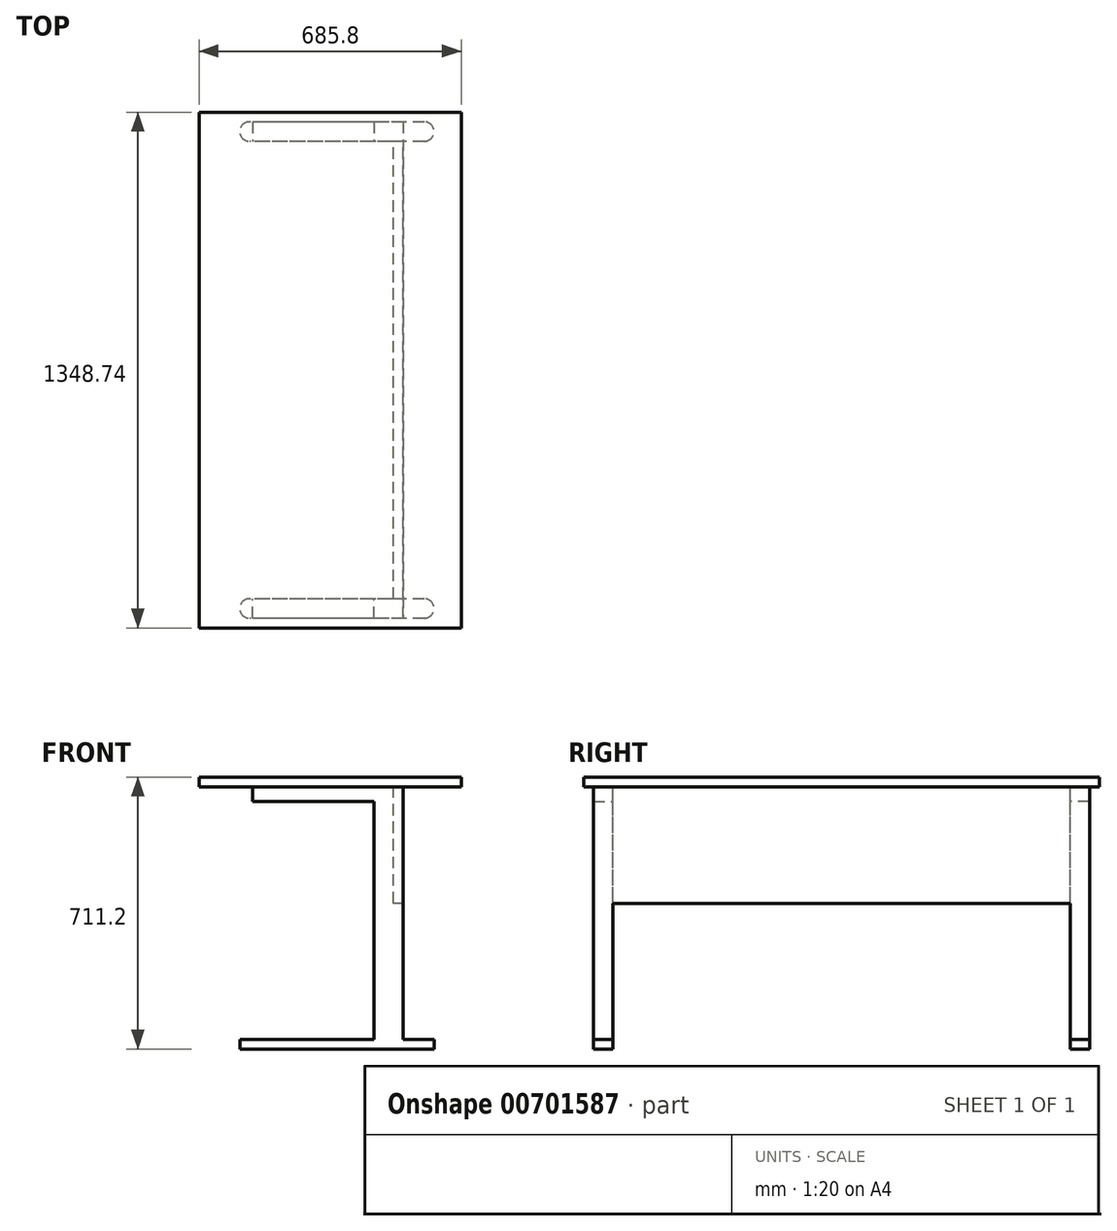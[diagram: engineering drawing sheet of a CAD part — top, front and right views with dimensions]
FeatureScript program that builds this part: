
annotation { "Feature Type Name" : "Feature", "Feature Type Description" : "" }
export const myFeature = defineFeature(function(context is Context, id is Id, definition is map)
    precondition{}
    {
        {
            var Q0;
            Q0=qCreatedBy(makeId("Top.planeOp"),FACE);
            var sketch = newSketch(context, id + "F0", { "sketchPlane" : qUnion([Q0])});
            skLineSegment(sketch, "E0.bottom", {"start": v(-342.9, 674.37) * mm, "end": v(342.9, 674.37) * mm});
            skLineSegment(sketch, "E0.top", {"start": v(-342.9, -674.37) * mm, "end": v(342.9, -674.37) * mm});
            skLineSegment(sketch, "E0.left", {"start": v(-342.9, 674.37) * mm, "end": v(-342.9, -674.37) * mm});
            skLineSegment(sketch, "E0.right", {"start": v(342.9, 674.37) * mm, "end": v(342.9, -674.37) * mm});
            skPoint(sketch, "E0.middle", {"position": v(0, 0) * mm});
            skSolve(sketch);
        }
        {
            var Q0;
            Q0=qSketchRegion(id+"F0",true);
            extrude(context, id + "F1", {"entities" : qUnion([Q0]), "depth" : 25.4 * mm, "offsetDistance" : 25.4 * mm});
        }
        {
            var Q0;
            Q0=makeQuery(id+"F1.opExtrude","CAP_FACE",FACE,{"disambiguationData":[OSD([sQuery(id+"F0.wireOp",EDGE,"E0.bottom"),sQuery(id+"F0.wireOp",EDGE,"E0.top"),sQuery(id+"F0.wireOp",EDGE,"E0.left"),sQuery(id+"F0.wireOp",EDGE,"E0.right")])],"isStart":true});
            var sketch = newSketch(context, id + "F2", { "sketchPlane" : qUnion([Q0])});
            skLineSegment(sketch, "E1", {"start": v(289.24, 0) * mm, "end": v(-342.9, 0) * mm});
            skLineSegment(sketch, "E2", {"start": v(-342.9, 0) * mm, "end": v(342.9, 0) * mm});
            skLineSegment(sketch, "E3.bottom", {"start": v(114.3, -648.97) * mm, "end": v(-203.2, -648.97) * mm});
            skLineSegment(sketch, "E3.top", {"start": v(114.3, -598.17) * mm, "end": v(-203.2, -598.17) * mm});
            skLineSegment(sketch, "E3.left", {"start": v(114.3, -648.97) * mm, "end": v(114.3, -598.17) * mm});
            skLineSegment(sketch, "E3.right", {"start": v(-203.2, -648.97) * mm, "end": v(-203.2, -598.17) * mm});
            skLineSegment(sketch, "E4.MirrorCS", {"start": v(114.3, 648.97) * mm, "end": v(-203.2, 648.97) * mm});
            skLineSegment(sketch, "E5.MirrorCS", {"start": v(114.3, 598.17) * mm, "end": v(-203.2, 598.17) * mm});
            skLineSegment(sketch, "E6.MirrorCS", {"start": v(-203.2, 648.97) * mm, "end": v(-203.2, 598.17) * mm});
            skLineSegment(sketch, "E7.MirrorCS", {"start": v(114.3, 648.97) * mm, "end": v(114.3, 598.17) * mm});
            skSolve(sketch);
        }
        {
            var Q0;
            Q0=qSketchRegion(id+"F2",true);
            extrude(context, id + "F3", {"entities" : qUnion([Q0]), "operationType" : NewBodyOperationType.ADD, "depth" : 38.1 * mm, "offsetDistance" : 25.4 * mm});
        }
        {
            var Q0;
            Q0=makeQuery(id+"F1.opExtrude","CAP_FACE",FACE,{"disambiguationData":[OSD([sQuery(id+"F0.wireOp",EDGE,"E0.bottom"),sQuery(id+"F0.wireOp",EDGE,"E0.top"),sQuery(id+"F0.wireOp",EDGE,"E0.left"),sQuery(id+"F0.wireOp",EDGE,"E0.right")])],"isStart":true});
            var sketch = newSketch(context, id + "F4", { "sketchPlane" : qUnion([Q0])});
            skLineSegment(sketch, "E8.bottom", {"start": v(114.3, -648.97) * mm, "end": v(190.5, -648.97) * mm});
            skLineSegment(sketch, "E8.top", {"start": v(114.3, -598.17) * mm, "end": v(190.5, -598.17) * mm});
            skLineSegment(sketch, "E8.left", {"start": v(114.3, -648.97) * mm, "end": v(114.3, -598.17) * mm});
            skLineSegment(sketch, "E8.right", {"start": v(190.5, -648.97) * mm, "end": v(190.5, -598.17) * mm});
            skLineSegment(sketch, "E9", {"start": v(298.65, 0) * mm, "end": v(-342.9, 0) * mm});
            skLineSegment(sketch, "E10", {"start": v(-342.9, 0) * mm, "end": v(342.9, 0) * mm});
            skLineSegment(sketch, "E11.MirrorCS", {"start": v(114.3, 648.97) * mm, "end": v(190.5, 648.97) * mm});
            skLineSegment(sketch, "E12.MirrorCS", {"start": v(114.3, 598.17) * mm, "end": v(190.5, 598.17) * mm});
            skLineSegment(sketch, "E13.MirrorCS", {"start": v(190.5, 648.97) * mm, "end": v(190.5, 598.17) * mm});
            skLineSegment(sketch, "E14", {"start": v(114.3, 623.57) * mm, "end": v(114.3, 648.97) * mm});
            skLineSegment(sketch, "E15", {"start": v(114.3, 609.27) * mm, "end": v(114.3, 598.17) * mm});
            skLineSegment(sketch, "E16", {"start": v(114.3, 609.27) * mm, "end": v(114.3, 623.57) * mm});
            skSolve(sketch);
        }
        {
            var Q0;
            Q0=makeQuery(id+"F4.imprint","IMPRINT",FACE,{"disambiguationData":[TD([[makeQuery(id+"F4.imprint","IMPRINT",EDGE,{"derivedFrom":sQuery(id+"F4.wireOp",EDGE,"E8.bottom")}),1.0]])]});
            var Q1;
            Q1=qSketchRegion(id+"F4",true);
            extrude(context, id + "F5", {"entities" : qUnion([Q0, Q1]), "operationType" : NewBodyOperationType.ADD, "depth" : 660.4 * mm, "offsetDistance" : 25.4 * mm});
        }
        {
            var Q0;
            Q0=makeQuery(id+"F5.opExtrude","CAP_FACE",FACE,{"disambiguationData":[OSD([sQuery(id+"F4.wireOp",EDGE,"E8.bottom"),sQuery(id+"F4.wireOp",EDGE,"E8.top"),sQuery(id+"F4.wireOp",EDGE,"E8.left"),sQuery(id+"F4.wireOp",EDGE,"E8.right")])],"isStart":false});
            var sketch = newSketch(context, id + "F6", { "sketchPlane" : qUnion([Q0])});
            skLineSegment(sketch, "E17.bottom", {"start": v(246.19, -598.17) * mm, "end": v(-211.01, -598.17) * mm});
            skLineSegment(sketch, "E17.top", {"start": v(246.19, -648.97) * mm, "end": v(-211.01, -648.97) * mm});
            skLineSegment(sketch, "E17.left", {"start": v(271.59, -623.57) * mm, "end": v(271.59, -623.57) * mm});
            skLineSegment(sketch, "E17.right", {"start": v(-236.41, -623.57) * mm, "end": v(-236.41, -623.57) * mm});
            skPoint(sketch, "E18.visualSharp", {"position": v(271.59, -648.97) * mm});
            skArc(sketch, "E18.filletArc", {"start": v(246.19, -648.97) * mm, "mid": v(264.15, -641.53) * mm, "end": v(271.59, -623.57) * mm});
            skPoint(sketch, "E19.visualSharp", {"position": v(271.59, -598.17) * mm});
            skArc(sketch, "E19.filletArc", {"start": v(271.59, -623.57) * mm, "mid": v(264.15, -605.6) * mm, "end": v(246.19, -598.17) * mm});
            skPoint(sketch, "E20.visualSharp", {"position": v(-236.41, -648.97) * mm});
            skArc(sketch, "E20.filletArc", {"start": v(-236.41, -623.57) * mm, "mid": v(-228.97, -641.53) * mm, "end": v(-211.01, -648.97) * mm});
            skPoint(sketch, "E21.visualSharp", {"position": v(-236.41, -598.17) * mm});
            skArc(sketch, "E21.filletArc", {"start": v(-211.01, -598.17) * mm, "mid": v(-228.97, -605.6) * mm, "end": v(-236.41, -623.57) * mm});
            skLineSegment(sketch, "E22", {"start": v(-361.07, 0) * mm, "end": v(355.78, 0) * mm});
            skArc(sketch, "E23.MirrorCS", {"start": v(-211.01, 598.17) * mm, "mid": v(-228.97, 605.6) * mm, "end": v(-236.41, 623.57) * mm});
            skPoint(sketch, "E24.MirrorP", {"position": v(-236.41, 648.97) * mm});
            skArc(sketch, "E25.MirrorCS", {"start": v(-236.41, 623.57) * mm, "mid": v(-228.97, 641.53) * mm, "end": v(-211.01, 648.97) * mm});
            skLineSegment(sketch, "E26.MirrorCS", {"start": v(246.19, 648.97) * mm, "end": v(-211.01, 648.97) * mm});
            skLineSegment(sketch, "E27.MirrorCS", {"start": v(246.19, 598.17) * mm, "end": v(-211.01, 598.17) * mm});
            skArc(sketch, "E28.MirrorCS", {"start": v(271.59, 623.57) * mm, "mid": v(264.15, 605.6) * mm, "end": v(246.19, 598.17) * mm});
            skArc(sketch, "E29.MirrorCS", {"start": v(246.19, 648.97) * mm, "mid": v(264.15, 641.53) * mm, "end": v(271.59, 623.57) * mm});
            skSolve(sketch);
        }
        {
            var Q0;
            Q0=qSketchRegion(id+"F6",true);
            extrude(context, id + "F7", {"entities" : qUnion([Q0]), "operationType" : NewBodyOperationType.ADD, "depth" : 25.4 * mm, "offsetDistance" : 25.4 * mm});
        }
        {
            var Q0;
            Q0=makeQuery(id+"F1.opExtrude","CAP_FACE",FACE,{"disambiguationData":[OSD([sQuery(id+"F0.wireOp",EDGE,"E0.bottom"),sQuery(id+"F0.wireOp",EDGE,"E0.top"),sQuery(id+"F0.wireOp",EDGE,"E0.left"),sQuery(id+"F0.wireOp",EDGE,"E0.right")])],"isStart":true});
            var sketch = newSketch(context, id + "F8", { "sketchPlane" : qUnion([Q0])});
            skLineSegment(sketch, "E30.bottom", {"start": v(165.1, 598.17) * mm, "end": v(190.5, 598.17) * mm});
            skLineSegment(sketch, "E30.top", {"start": v(165.1, -598.17) * mm, "end": v(190.5, -598.17) * mm});
            skLineSegment(sketch, "E30.left", {"start": v(165.1, 598.17) * mm, "end": v(165.1, -598.17) * mm});
            skLineSegment(sketch, "E30.right", {"start": v(190.5, 598.17) * mm, "end": v(190.5, -598.17) * mm});
            skSolve(sketch);
        }
        {
            var Q0;
            Q0=qSketchRegion(id+"F8",true);
            extrude(context, id + "F9", {"entities" : qUnion([Q0]), "operationType" : NewBodyOperationType.ADD, "depth" : 304.8 * mm, "offsetDistance" : 25.4 * mm});
        }
    });
